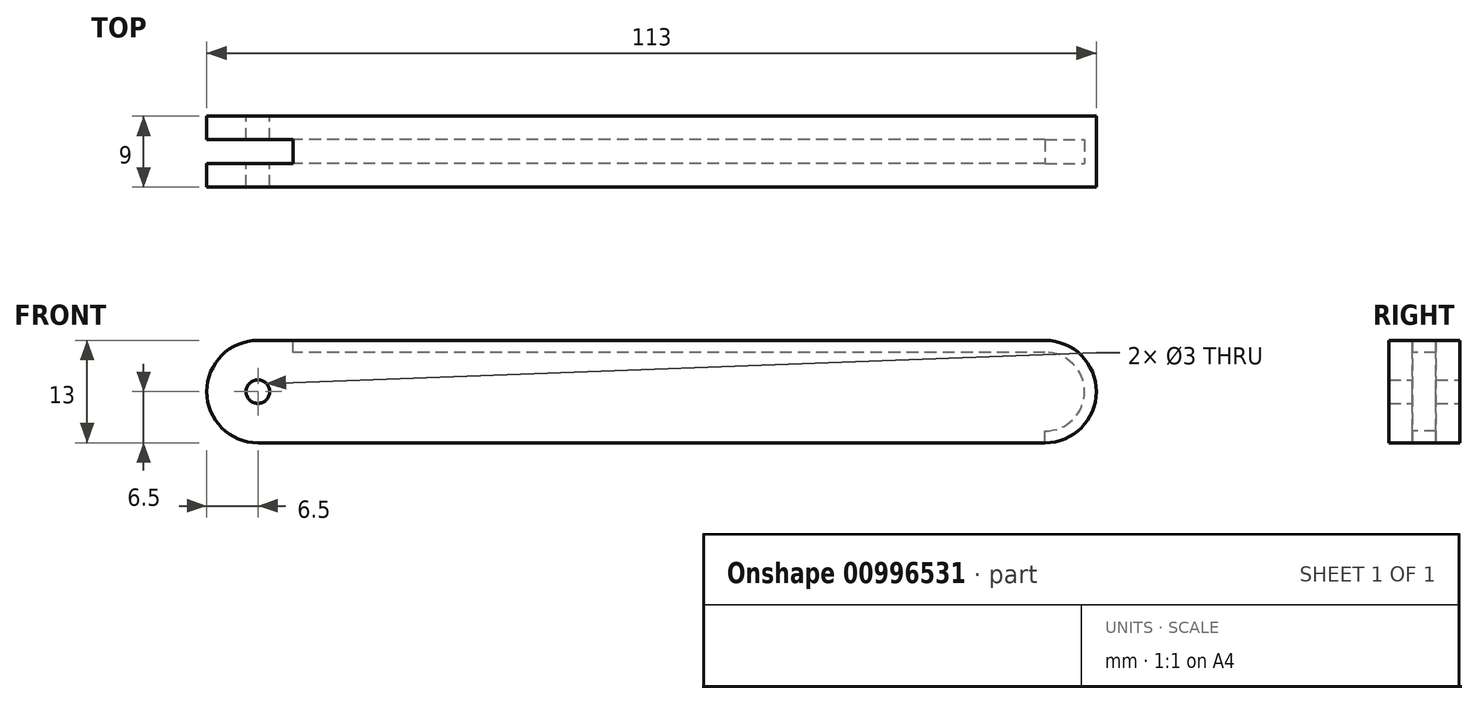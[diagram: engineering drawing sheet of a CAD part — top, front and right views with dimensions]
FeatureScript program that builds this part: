
annotation { "Feature Type Name" : "Feature", "Feature Type Description" : "" }
export const myFeature = defineFeature(function(context is Context, id is Id, definition is map)
    precondition{}
    {
        {
            var Q0;
            Q0=qCreatedBy(makeId("Front.planeOp"),FACE);
            var sketch = newSketch(context, id + "F0", { "sketchPlane" : qUnion([Q0])});
            skLineSegment(sketch, "E0.bottom", {"start": v(50, -6.5) * mm, "end": v(-50, -6.5) * mm});
            skLineSegment(sketch, "E0.top", {"start": v(50, 6.5) * mm, "end": v(-50, 6.5) * mm});
            skLineSegment(sketch, "E0.left", {"start": v(50, -6.5) * mm, "end": v(50, 6.5) * mm});
            skLineSegment(sketch, "E0.right", {"start": v(-50, -6.5) * mm, "end": v(-50, 6.5) * mm});
            skPoint(sketch, "E0.middle", {"position": v(0, 0) * mm});
            skArc(sketch, "E1", {"start": v(-50, 6.5) * mm, "mid": v(-56.5, 0) * mm, "end": v(-50, -6.5) * mm});
            skArc(sketch, "E2", {"start": v(50, -6.5) * mm, "mid": v(56.5, 0) * mm, "end": v(50, 6.5) * mm});
            skCircle(sketch, "E3", {"center": v(-50, 0) * mm, "radius": 1.5 * mm});
            skLineSegment(sketch, "E4.0", {"start": v(50, 5) * mm, "end": v(-50, 5) * mm});
            skArc(sketch, "E4.1", {"start": v(50, -5) * mm, "mid": v(55, 0) * mm, "end": v(50, 5) * mm});
            skLineSegment(sketch, "E5", {"start": v(-45.5, 5) * mm, "end": v(-45.5, 6.5) * mm});
            skLineSegment(sketch, "E6", {"start": v(-45.5, 6.5) * mm, "end": v(-50, 6.5) * mm});
            skSolve(sketch);
        }
        {
            var Q0;
            {var subQ0=sQuery(id+"F0.wireOp",EDGE,"E2");Q0=makeQuery(id+"F0.imprint","IMPRINT",FACE,{"disambiguationData":[TD([[makeQuery(id+"F0.imprint","IMPRINT",EDGE,{"derivedFrom":subQ0}),1.0]])]});}
            var Q1;
            {var subQ0=sQuery(id+"F0.wireOp",EDGE,"E0.top");Q1=makeQuery(id+"F0.imprint","IMPRINT",FACE,{"disambiguationData":[TD([[makeQuery(id+"F0.imprint","IMPRINT",EDGE,{"derivedFrom":subQ0}),1.0]])]});}
            var Q2;
            {var subQ0=sQuery(id+"F0.wireOp",EDGE,"E4.1");Q2=makeQuery(id+"F0.imprint","IMPRINT",FACE,{"disambiguationData":[TD([[makeQuery(id+"F0.imprint","IMPRINT",EDGE,{"derivedFrom":subQ0}),1.0]])]});}
            var Q3;
            {var subQ4=sQuery(id+"F0.wireOp",EDGE,"E0.bottom");Q3=makeQuery(id+"F0.imprint","IMPRINT",FACE,{"disambiguationData":[TD([[makeQuery(id+"F0.imprint","IMPRINT",EDGE,{"derivedFrom":subQ4}),-1.0]])]});}
            var Q4;
            {var subQ0=sQuery(id+"F0.wireOp",EDGE,"E1");Q4=makeQuery(id+"F0.imprint","IMPRINT",FACE,{"disambiguationData":[TD([[makeQuery(id+"F0.imprint","IMPRINT",EDGE,{"derivedFrom":subQ0}),1.0]])]});}
            var Q5;
            {var subQ4=sQuery(id+"F0.wireOp",EDGE,"E5");Q5=makeQuery(id+"F0.imprint","IMPRINT",FACE,{"disambiguationData":[TD([[makeQuery(id+"F0.imprint","IMPRINT",EDGE,{"derivedFrom":subQ4}),1.0]])]});}
            extrude(context, id + "F1", {"entities" : qUnion([Q0, Q1, Q2, Q3, Q4, Q5]), "endBound" : BoundingType.SYMMETRIC, "depth" : 9 * mm, "offsetDistance" : 25 * mm});
        }
        {
            var Q0;
            {var subQ4=sQuery(id+"F0.wireOp",EDGE,"E0.bottom");Q0=makeQuery(id+"F0.imprint","IMPRINT",FACE,{"disambiguationData":[TD([[makeQuery(id+"F0.imprint","IMPRINT",EDGE,{"derivedFrom":subQ4}),-1.0]])]});}
            var Q1;
            {var subQ0=sQuery(id+"F0.wireOp",EDGE,"E1");Q1=makeQuery(id+"F0.imprint","IMPRINT",FACE,{"disambiguationData":[TD([[makeQuery(id+"F0.imprint","IMPRINT",EDGE,{"derivedFrom":subQ0}),1.0]])]});}
            var Q2;
            {var subQ0=sQuery(id+"F0.wireOp",EDGE,"E4.1");Q2=makeQuery(id+"F0.imprint","IMPRINT",FACE,{"disambiguationData":[TD([[makeQuery(id+"F0.imprint","IMPRINT",EDGE,{"derivedFrom":subQ0}),1.0]])]});}
            var Q3;
            {var subQ4=sQuery(id+"F0.wireOp",EDGE,"E5");Q3=makeQuery(id+"F0.imprint","IMPRINT",FACE,{"disambiguationData":[TD([[makeQuery(id+"F0.imprint","IMPRINT",EDGE,{"derivedFrom":subQ4}),1.0]])]});}
            extrude(context, id + "F2", {"entities" : qUnion([Q0, Q1, Q2, Q3]), "operationType" : NewBodyOperationType.REMOVE, "endBound" : BoundingType.SYMMETRIC, "oppositeDirection" : true, "depth" : 3 * mm, "offsetDistance" : 25 * mm});
        }
    });
